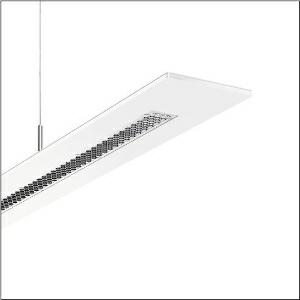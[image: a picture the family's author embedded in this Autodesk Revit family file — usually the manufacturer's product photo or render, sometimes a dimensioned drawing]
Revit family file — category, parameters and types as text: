
# Revit family: arktika_r__21_duo_5mb252dl60840_f6f7
name_source: partatom
category: Lighting Fixtures
units: mm (PartAtom-declared; Revit-internal decimal feet)

## family parameters
Cut with Voids When Loaded = No
Host = Face
Light Source = No
Part Type = Normal
Room Calculation Point = No
Round Connector Dimension = Use Diameter
Shared = No

## types (1)
- --- (1 x LED 4000K / CRI = 80 (unbekannt), 8800 lm, 4000K)
    Apparent Load = 67 VA
    CIE Flux Codes = 81 100 100 79 100
    Color Rendering = 80
    Color Temperature = 4000K
    Default Elevation = 1800 mm
    Description = Arktika® 21 duo, office luminaire, primary anti-glare with honeycomb louvre, of plastic, aluminium vaporised, highly specular, light emission: direct/indirect distribution, primary light characteristic: symmetric, installation type: suspended mounting, LED, rated luminous flux: 8.800lm, luminous efficacy: 132lm/W, light colour: 840, colour temperature: 4000K, control gear: DALI, with terminal, 3+2-pole, max. 2.5mm², mains connection: 220..240V, AC, 50/60Hz, rated input power: 67W, housing, of aluminium, powder-coated, traffic white (RAL 9016), 2-length, length: 2.280mm, width: 120mm, height: 8mm, protection rating (complete): IP20, insulation class (complete): insulation class II (safety insulation), certification: CE, packaging unit: 1 piece
    Height = 8 mm  [stored 0.0262467 ft]
    Lamp = 1 x LED 4000K / CRI >= 80 (unbekannt)
    Lamp Light Flux = 8800 lm
    Lamp count = 1
    Length = 2280 mm
    Luminous efficacy = 132 lm/W
    Manufacturer = Siteco
    ModVariant = No
    Model = 5MB252DL60840
    Mounting Place = Ceiling
    Mounting Type = Pendant
    Number of Poles = 1
    OnlyDefault = Yes
    Power Factor = 1
    Product Name = Arktika® 21 duo
    Product group = office luminaire | ceiling pendant
    ProductGroupID = 904
    Protection Class = Protection class II
    Protection Degree = IP 20
    RLX_Detail_Level = 1
    RLX_Emergency_Light_Flux = 0 lm
    RLX_Emergency_Type = 0
    RLX_Emergency_Type_DB = No
    RlxData = <blob elided: 39841 chars, md5=5731a562>
    Socket = socket
    Standby Power = 0 W
    System Light Flux = 8800 lm
    System Power = 67 W
    Type Comments = factory setting: luminous flux: 100 % | dim-lin: 254 | 1330 mA
    Type Image = l_1006128.jpg
    URL = http://relux.com
    VarID = @adj_202876
    Voltage = 0 V
    Weight = 0.00 kg
    Width = 120 mm

note: [stored X ft] marks values corroborated as IEEE doubles in the binary element streams (Revit-internal decimal feet)

## geometry (parser evidence)
native form markers: Blend x4, Sweep x13
no freeform markers — native parametric forms only
